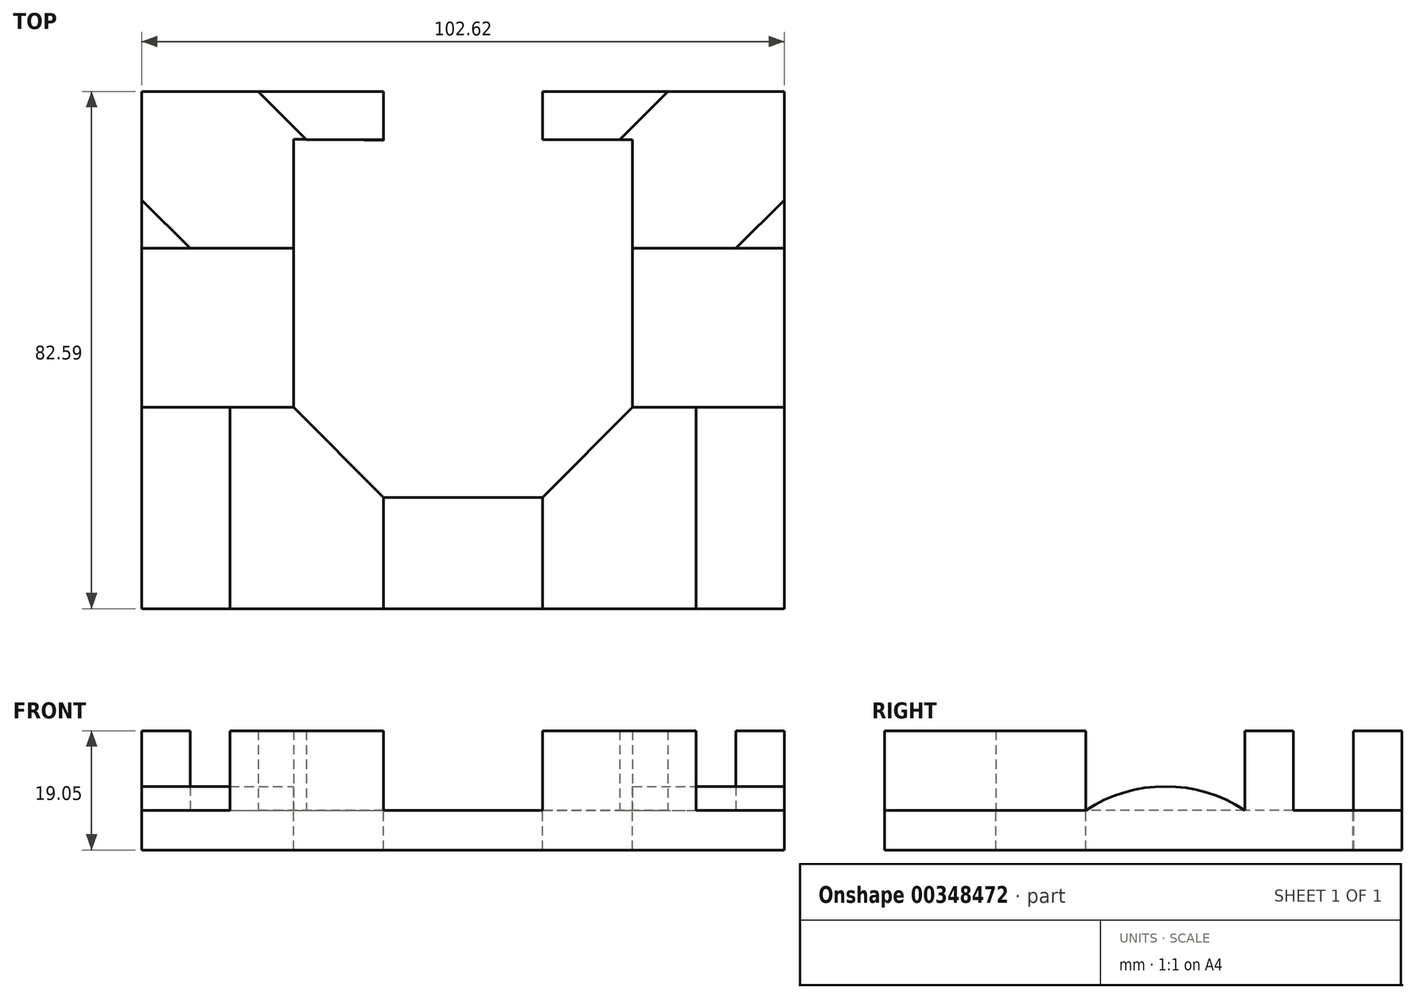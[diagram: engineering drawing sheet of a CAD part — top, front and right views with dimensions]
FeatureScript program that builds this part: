
annotation { "Feature Type Name" : "Feature", "Feature Type Description" : "" }
export const myFeature = defineFeature(function(context is Context, id is Id, definition is map)
    precondition{}
    {
        {
            var Q0;
            Q0=qCreatedBy(makeId("Top.planeOp"),FACE);
            var sketch = newSketch(context, id + "F0", { "sketchPlane" : qUnion([Q0])});
            skLineSegment(sketch, "E0", {"start": v(0, 0) * mm, "end": v(10.16, 0) * mm});
            skLineSegment(sketch, "E1", {"start": v(10.16, 0) * mm, "end": v(24.53, -14.37) * mm});
            skLineSegment(sketch, "E2", {"start": v(24.53, -14.37) * mm, "end": v(24.53, -32.15) * mm});
            skLineSegment(sketch, "E3", {"start": v(24.53, -32.15) * mm, "end": v(0, -32.15) * mm});
            skLineSegment(sketch, "E4", {"start": v(0, -32.15) * mm, "end": v(0, 0) * mm});
            skLineSegment(sketch, "E5", {"start": v(4.5, 50.44) * mm, "end": v(12.23, 42.72) * mm});
            skLineSegment(sketch, "E6", {"start": v(12.23, 42.72) * mm, "end": v(24.53, 42.72) * mm});
            skLineSegment(sketch, "E7", {"start": v(62.23, 42.72) * mm, "end": v(69.95, 50.44) * mm});
            skLineSegment(sketch, "E8", {"start": v(69.95, 50.44) * mm, "end": v(49.93, 50.44) * mm});
            skLineSegment(sketch, "E9", {"start": v(64.3, 0) * mm, "end": v(74.46, 0) * mm});
            skLineSegment(sketch, "E10", {"start": v(74.46, 0) * mm, "end": v(74.46, -32.15) * mm});
            skLineSegment(sketch, "E11", {"start": v(74.46, -32.15) * mm, "end": v(49.93, -32.15) * mm});
            skLineSegment(sketch, "E12", {"start": v(49.93, -32.15) * mm, "end": v(49.93, -14.37) * mm});
            skLineSegment(sketch, "E13", {"start": v(49.93, -14.37) * mm, "end": v(64.3, 0) * mm});
            skLineSegment(sketch, "E14", {"start": v(80.8, 25.4) * mm, "end": v(88.53, 25.4) * mm});
            skLineSegment(sketch, "E15", {"start": v(88.53, 25.4) * mm, "end": v(88.53, 33.12) * mm});
            skLineSegment(sketch, "E16", {"start": v(88.53, 33.12) * mm, "end": v(80.8, 25.4) * mm});
            skLineSegment(sketch, "E17.MirrorCS", {"start": v(-6.35, 25.4) * mm, "end": v(-14.07, 25.4) * mm});
            skLineSegment(sketch, "E18.MirrorCS", {"start": v(-14.07, 25.4) * mm, "end": v(-14.07, 33.12) * mm});
            skLineSegment(sketch, "E19.MirrorCS", {"start": v(-14.07, 33.12) * mm, "end": v(-6.35, 25.4) * mm});
            skLineSegment(sketch, "E20", {"start": v(24.53, 50.44) * mm, "end": v(4.5, 50.44) * mm});
            skLineSegment(sketch, "E21", {"start": v(49.93, 42.72) * mm, "end": v(62.23, 42.72) * mm});
            skLineSegment(sketch, "E22", {"start": v(24.53, 42.72) * mm, "end": v(24.53, 50.44) * mm});
            skLineSegment(sketch, "E23", {"start": v(49.93, 42.72) * mm, "end": v(49.93, 50.44) * mm});
            skSolve(sketch);
        }
        {
            var Q0;
            Q0 = qSketchRegion(id + "F0", true);
            extrude(context, id + "F1", {"entities" : qUnion([Q0]), "depth" : 12.7 * mm});
        }
        {
            var Q0;
            Q0=qCreatedBy(makeId("Top.planeOp"),FACE);
            var sketch = newSketch(context, id + "F2", { "sketchPlane" : qUnion([Q0])});
            skLineSegment(sketch, "E24.bottom", {"start": v(-14.07, 50.44) * mm, "end": v(24.53, 50.44) * mm});
            skLineSegment(sketch, "E24.top", {"start": v(-14.07, -32.15) * mm, "end": v(88.53, -32.15) * mm});
            skLineSegment(sketch, "E24.left", {"start": v(-14.07, 50.44) * mm, "end": v(-14.07, -32.15) * mm});
            skLineSegment(sketch, "E24.right", {"start": v(88.53, 50.44) * mm, "end": v(88.53, -32.15) * mm});
            skLineSegment(sketch, "E25", {"start": v(49.93, 50.44) * mm, "end": v(88.53, 50.44) * mm});
            skLineSegment(sketch, "E26", {"start": v(24.53, 50.44) * mm, "end": v(24.53, 42.65) * mm});
            skLineSegment(sketch, "E27", {"start": v(24.53, -14.37) * mm, "end": v(49.93, -14.37) * mm});
            skLineSegment(sketch, "E28", {"start": v(49.93, 42.72) * mm, "end": v(49.93, 50.44) * mm});
            skLineSegment(sketch, "E29", {"start": v(10.16, 0) * mm, "end": v(10.16, 42.8) * mm});
            skLineSegment(sketch, "E30", {"start": v(10.16, 42.8) * mm, "end": v(24.53, 42.65) * mm});
            skLineSegment(sketch, "E31", {"start": v(49.93, 42.72) * mm, "end": v(64.3, 42.72) * mm});
            skLineSegment(sketch, "E32", {"start": v(64.3, 42.72) * mm, "end": v(64.3, 0) * mm});
            skLineSegment(sketch, "E33", {"start": v(10.16, 0) * mm, "end": v(24.53, -14.37) * mm});
            skLineSegment(sketch, "E34", {"start": v(64.3, 0) * mm, "end": v(49.93, -14.37) * mm});
            skSolve(sketch);
        }
        {
            var Q0;
            Q0 = qSketchRegion(id + "F2", true);
            extrude(context, id + "F3", {"entities" : qUnion([Q0]), "oppositeDirection" : true, "depth" : 6.35 * mm});
        }
        {
            var Q0;
            Q0=makeQuery(id+"F3.opExtrude","SWEPT_FACE",FACE,{"disambiguationData":[OSD([sQuery(id+"F2.wireOp",EDGE,"E24.right")])]});
            var sketch = newSketch(context, id + "F4", { "sketchPlane" : qUnion([Q0])});
            skPoint(sketch, "E35", {"position": v(25.4, 0) * mm});
            skArc(sketch, "E36", {"start": v(25.4, 0) * mm, "mid": v(12.7, 3.81) * mm, "end": v(0, 0) * mm});
            skPoint(sketch, "E37", {"position": v(12.7, 0) * mm});
            skPoint(sketch, "E38", {"position": v(12.7, 3.81) * mm});
            skLineSegment(sketch, "E39", {"start": v(0, 0) * mm, "end": v(25.4, 0) * mm});
            skSolve(sketch);
        }
        {
            var Q0;
            Q0 = qSketchRegion(id + "F4", true);
            extrude(context, id + "F5", {"entities" : qUnion([Q0]), "operationType" : NewBodyOperationType.ADD, "oppositeDirection" : true, "depth" : 102.62 * mm});
        }
        {
            var Q0;
            {var subQ0=sQuery(id+"F2.wireOp",EDGE,"E25");var subQ1=sQuery(id+"F2.wireOp",EDGE,"E28");var subQ3=sQuery(id+"F2.wireOp",EDGE,"E31");var subQ5=sQuery(id+"F2.wireOp",EDGE,"E24.right");var subQ6=sQuery(id+"F2.wireOp",EDGE,"E32");Q0=makeQuery(id+"F5.boolean.opBoolean","SPLIT",FACE,{"disambiguationData":[TD([makeQuery(id+"F1.opExtrude","SWEPT_FACE",FACE,{"disambiguationData":[OSD([sQuery(id+"F0.wireOp",EDGE,"E14")])]})])],"derivedFrom":makeQuery(id+"F3.opExtrude","CAP_FACE",FACE,{"disambiguationData":[OSD([sQuery(id+"F2.wireOp",EDGE,"E24.bottom"),sQuery(id+"F2.wireOp",EDGE,"E24.top"),sQuery(id+"F2.wireOp",EDGE,"E24.left"),subQ5,subQ0,sQuery(id+"F2.wireOp",EDGE,"E26"),sQuery(id+"F2.wireOp",EDGE,"E27"),subQ1,sQuery(id+"F2.wireOp",EDGE,"E29"),sQuery(id+"F2.wireOp",EDGE,"E30"),subQ3,subQ6,sQuery(id+"F2.wireOp",EDGE,"E33"),sQuery(id+"F2.wireOp",EDGE,"E34")])],"isStart":true})});}
            var sketch = newSketch(context, id + "F6", { "sketchPlane" : qUnion([Q0])});
            skLineSegment(sketch, "E40.bottom", {"start": v(64.3, 25.4) * mm, "end": v(10.16, 25.4) * mm});
            skLineSegment(sketch, "E40.top", {"start": v(64.3, 0) * mm, "end": v(10.16, 0) * mm});
            skLineSegment(sketch, "E40.left", {"start": v(64.3, 25.4) * mm, "end": v(64.3, 0) * mm});
            skLineSegment(sketch, "E40.right", {"start": v(10.16, 25.4) * mm, "end": v(10.16, 0) * mm});
            skSolve(sketch);
        }
        {
            var Q0;
            Q0 = qSketchRegion(id + "F6", true);
            extrude(context, id + "F7", {"entities" : qUnion([Q0]), "operationType" : NewBodyOperationType.REMOVE, "depth" : 6.35 * mm});
        }
    });
